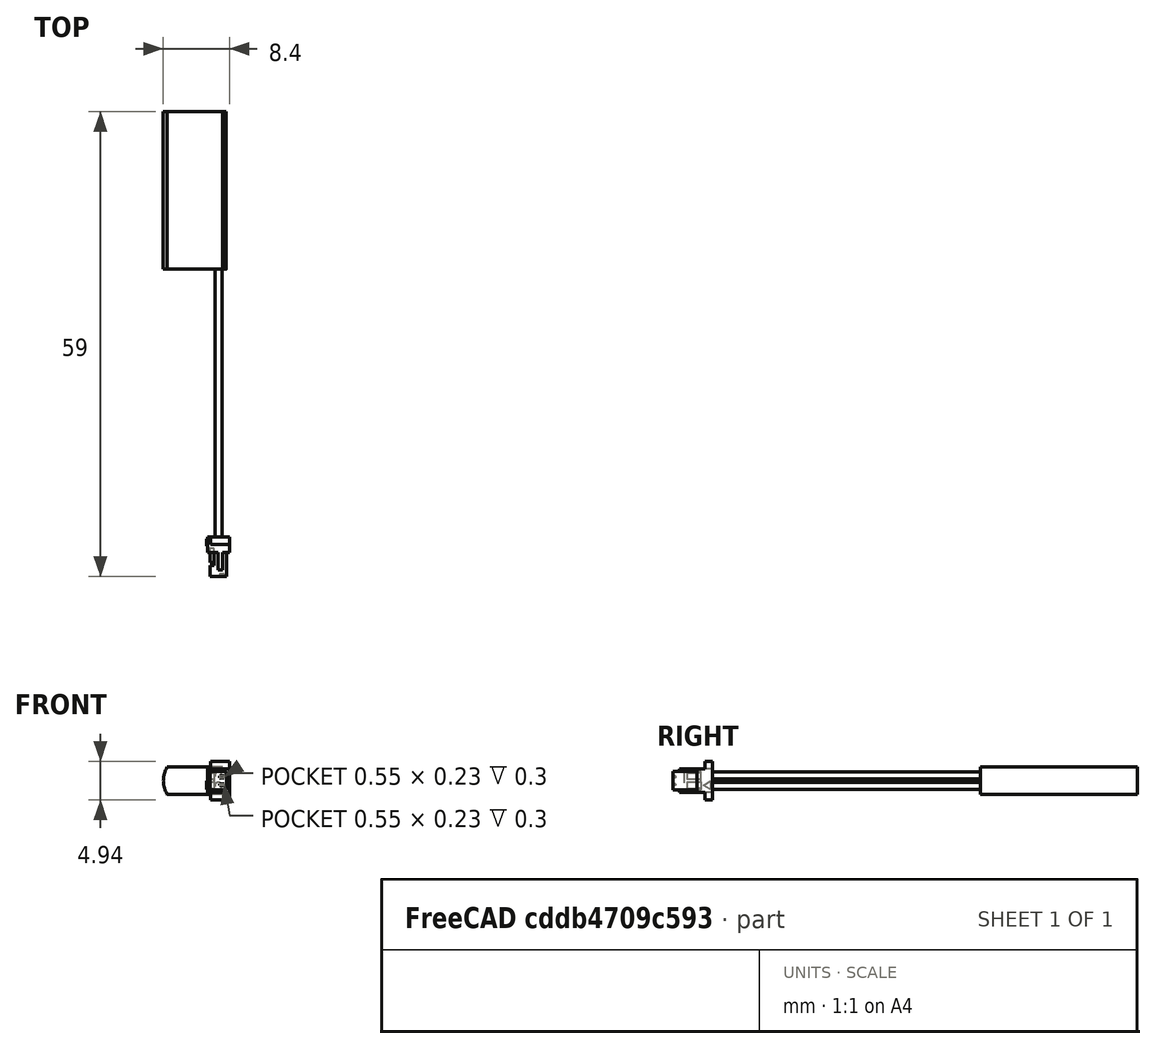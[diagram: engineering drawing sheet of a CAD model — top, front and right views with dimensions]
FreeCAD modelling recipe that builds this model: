
FCSTD DOCUMENT  (FreeCAD 2021.519R24301 +3652 (Git))
Label: ASR00072_40mAh
License: Other
objects: TechDraw::DrawViewDimension×4, Sketcher::SketchObject×3, PartDesign::Pad×3, TechDraw::DrawViewPart×2, TechDraw::DrawViewAnnotation×2, PartDesign::Pocket×1, PartDesign::Mirrored×1, PartDesign::Body×1, Part::Feature×1, Part::MultiFuse×1, TechDraw::DrawSVGTemplate×1, TechDraw::DrawPage×1, Mesh::Feature×1
note: 21 computed .brp shape members not serialized (recipe doc carries the construction recipe); baked Part::Feature solids carry a one-line shape summary decoded from their .brp

FEATURE [Sketcher::SketchObject] Sketch
  FullyConstrained = true
  MapMode = 5
  Support = -> [XY_Plane]
  sketch-geometry (4):
    g0: LineSegment StartX=-4 StartY=10 StartZ=0 EndX=4 EndY=10 EndZ=0
    g1: LineSegment StartX=4 StartY=10 StartZ=0 EndX=4 EndY=-10 EndZ=0
    g2: LineSegment StartX=4 StartY=-10 StartZ=0 EndX=-4 EndY=-10 EndZ=0
    g3: LineSegment StartX=-4 StartY=-10 StartZ=0 EndX=-4 EndY=10 EndZ=0
  constraints (10):
    c: Coincident(g0,g1)
    c: Coincident(g1,g2)
    c: Coincident(g2,g3)
    c: Coincident(g3,g0)
    c: Horizontal(g2)
    c: Vertical(g1)
    c: Symmetric(g0,g2,g-1)
    c: Symmetric(g0,g0,g-2)
    c: DistanceX(g0,g0) = 8
    c: DistanceY(g3,g3) = 20
FEATURE [PartDesign::Pad] Pad
  ClaimChildren = false
  Direction = (1,1,1)
  Fit = 0
  FitJoin = 0
  InnerFit = 0
  InnerFitJoin = 0
  InnerTaperAngle = 0
  InnerTaperAngleRev = 0
  Length = 3.5
  Length2 = 100
  Midplane = true
  NewSolid = false
  Profile = -> Sketch
  Suppress = false
  Type = 0
FEATURE [Sketcher::SketchObject] Sketch001
  ExternalGeometry = -> [Pad]
  FullyConstrained = true
  MapMode = 5
  Placement = pos=(0,10,0) rot=(0,0.707107,0.707107;3.14159rad)
  Support = -> [Pad]
  sketch-geometry (5):
    g0: ArcOfCircle CenterX=-0.6875 CenterY=-4e-16 CenterZ=0 NormalX=0 NormalY=0 NormalZ=1 AngleXU=0 Radius=3.3125 StartAngle=2.58499 EndAngle=3.69819
    g1: LineSegment [constr] StartX=-3.5 StartY=-1.75 StartZ=0 EndX=-3.5 EndY=1.75 EndZ=0
    g2: LineSegment StartX=-3.5 StartY=-1.75 StartZ=0 EndX=-5 EndY=-1.75 EndZ=0
    g3: LineSegment StartX=-3.5 StartY=1.75 StartZ=0 EndX=-5 EndY=1.75 EndZ=0
    g4: LineSegment StartX=-5 StartY=1.75 StartZ=0 EndX=-5 EndY=-1.75 EndZ=0
  constraints (15):
    c: PointOnObject(g0,g-5)
    c: PointOnObject(g0,g-4)
    c: Tangent(g0,g-3)
    c: Coincident(g1,g0)
    c: Coincident(g1,g0)
    c: Vertical(g1)
    c: Coincident(g2,g0)
    c: Horizontal(g2)
    c: Coincident(g3,g0)
    c: Horizontal(g3)
    c: Coincident(g4,g3)
    c: Coincident(g4,g2)
    c: Vertical(g4)
    c: DistanceX(g3,g-4) = 1
    c: DistanceX(g-4,g0) = 0.5
FEATURE [PartDesign::Pocket] Pocket
  BaseFeature = -> Pad
  ClaimChildren = false
  Fit = 0
  FitJoin = 0
  InnerFit = 0
  InnerFitJoin = 0
  InnerTaperAngle = 0
  InnerTaperAngleRev = 0
  Length = 5
  Length2 = 100
  NewSolid = false
  Profile = -> Sketch001
  Suppress = false
  Type = 1
FEATURE [PartDesign::Mirrored] Mirrored
  BaseFeature = -> Pocket
  CopyShape = true
  MirrorPlane = -> Sketch001 [V_Axis]
  NewSolid = false
  OriginalSubs = -> [Pocket]
  Originals = -> [Pocket]
  ParallelTransform = true
  SubTransform = true
  Suppress = false
FEATURE [PartDesign::Pad] Pad001
  BaseFeature = -> Mirrored
  ClaimChildren = false
  Direction = (1,1,1)
  Fit = 0
  FitJoin = 0
  InnerFit = 0
  InnerFitJoin = 0
  InnerTaperAngle = 0
  InnerTaperAngleRev = 0
  Length = 7.85
  Length2 = 100
  NewSolid = false
  Profile = -> Mirrored [Face8]
  Reversed = true
  Suppress = false
  Type = 0
FEATURE [Sketcher::SketchObject] Sketch002
  ExternalGeometry = -> [Pad001]
  FullyConstrained = true
  MapMode = 5
  Placement = pos=(0,-10,0) rot=(1,0,0;1.5708rad)
  Support = -> [Pad001]
  sketch-geometry (6):
    g0: Circle CenterX=3 CenterY=-0.65 CenterZ=0 NormalX=0 NormalY=0 NormalZ=1 AngleXU=0 Radius=0.45
    g1: Circle CenterX=3 CenterY=0.65 CenterZ=0 NormalX=0 NormalY=0 NormalZ=1 AngleXU=0 Radius=0.45
    g2: LineSegment [constr] StartX=3 StartY=0.65 StartZ=0 EndX=3 EndY=-0.65 EndZ=0
    g3: GeomPoint [constr] X=3 Y=-1.1 Z=0
    g4: GeomPoint [constr] X=3 Y=1.1 Z=0
    g5: LineSegment [constr] StartX=3 StartY=-0.65 StartZ=0 EndX=3.45 EndY=-0.65 EndZ=0
  constraints (13):
    c: Coincident(g2,g1)
    c: Coincident(g2,g0)
    c: Equal(g0,g1)
    c: Diameter(g0) = 0.9
    c: Symmetric(g0,g1,g-1)
    c: PointOnObject(g3,g2)
    c: PointOnObject(g4,g1)
    c: Symmetric(g3,g4,g-1)
    c: DistanceY(g-3,g3) = 0.65
    c: Coincident(g5,g0)
    c: PointOnObject(g5,g0)
    c: Horizontal(g5)
    c: DistanceX(g5,g-3) = 0.05
FEATURE [PartDesign::Pad] Pad002
  BaseFeature = -> Pad001
  ClaimChildren = false
  Direction = (1,1,1)
  Fit = 0
  FitJoin = 0
  InnerFit = 0
  InnerFitJoin = 0
  InnerTaperAngle = 0
  InnerTaperAngleRev = 0
  Length = 34
  Length2 = 100
  NewSolid = false
  Profile = -> Sketch002
  Suppress = false
  Type = 0
FEATURE [PartDesign::Body] Body
  AutoGroupSolids = false
  ExportMode = 0
  Group = -> [Sketch,Pad,Sketch001,Pocket,Mirrored,Pad001,Sketch002,Pad002]
  Origin = -> Origin
  Tip = -> Pad002
  _ExportChildren = -> [Pad,Pocket,Mirrored,Pad001,Pad002]
  _GroupVersion = 1
FEATURE [Part::Feature] Solid  label="Body007"
  Placement = pos=(1.71545,-46,8.5e-15) rot=(0,0,1;0rad)
  shape: bbox 2.9 x 5 x 4.94 mm, 60 faces (baked)
FEATURE [Part::MultiFuse] Fusion
  Shapes = -> [Body,Solid]
FEATURE [TechDraw::DrawSVGTemplate] Template
  Height = 210
  Orientation = 1
  Width = 297
FEATURE [TechDraw::DrawViewPart] View
  CoarseView = false
  Direction = (0,0,1)
  Focus = 100
  HardHidden = false
  IsoCount = 0
  IsoHidden = false
  IsoVisible = false
  LockPosition = false
  Perspective = false
  Rotation = 180
  Scale = 1.855
  ScaleType = 0
  SeamHidden = false
  SeamVisible = true
  SmoothHidden = false
  SmoothVisible = true
  Source = -> [Fusion]
  X = 178.5
  XDirection = (1,0,0)
  Y = 105
FEATURE [TechDraw::DrawViewPart] View001
  CoarseView = false
  Direction = (-1,0,0)
  Focus = 100
  HardHidden = false
  IsoCount = 0
  IsoHidden = false
  IsoVisible = false
  LockPosition = false
  Perspective = false
  Rotation = 90
  Scale = 1.855
  ScaleType = 0
  SeamHidden = false
  SeamVisible = true
  SmoothHidden = false
  SmoothVisible = true
  Source = -> [Fusion]
  X = 118.5
  XDirection = (0,-1,0)
  Y = 105
FEATURE [TechDraw::DrawViewAnnotation] Annotation
  Font = MS Shell Dlg 2
  LineSpace = 80
  LockPosition = false
  MaxWidth = -1
  Rotation = 0
  ScaleType = 0
  Text = SIDE VIEW
  TextSize = 6
  TextStyle = 0
  X = 118.5
  Y = 162
FEATURE [TechDraw::DrawViewAnnotation] Annotation001
  Font = MS Shell Dlg 2
  LineSpace = 80
  LockPosition = false
  MaxWidth = -1
  Rotation = 0
  ScaleType = 0
  Text = TOP VIEW
  TextSize = 6
  TextStyle = 0
  X = 178.5
  Y = 162
FEATURE [TechDraw::DrawViewDimension] Dimension
  Arbitrary = false
  ArbitraryTolerances = false
  EqualTolerance = true
  FormatSpec = %.1f
  FormatSpecOverTolerance = %+.1f
  FormatSpecUnderTolerance = %+.1f
  Inverted = false
  LockPosition = false
  MeasureType = 1
  OverTolerance = 0.5
  References2D = -> [View001]
  Rotation = 0
  ScaleType = 0
  TheoreticalExact = false
  Type = 1
  UnderTolerance = -0.5
  X = -31
  Y = -59
FEATURE [TechDraw::DrawViewDimension] Dimension001
  Arbitrary = false
  ArbitraryTolerances = false
  EqualTolerance = true
  FormatSpec = %.1f
  FormatSpecOverTolerance = %+.1f
  FormatSpecUnderTolerance = %+.1f
  Inverted = false
  LockPosition = false
  MeasureType = 1
  OverTolerance = 2
  References2D = -> [View]
  Rotation = 0
  ScaleType = 0
  TheoreticalExact = false
  Type = 1
  UnderTolerance = -2
  X = 24.371
  Y = -59
FEATURE [TechDraw::DrawViewDimension] Dimension002
  Arbitrary = false
  ArbitraryTolerances = false
  EqualTolerance = true
  FormatSpec = %.1f
  FormatSpecOverTolerance = %+.1f
  FormatSpecUnderTolerance = %+.1f
  Inverted = false
  LockPosition = false
  MeasureType = 1
  OverTolerance = 3
  References2D = -> [View]
  Rotation = 0
  ScaleType = 0
  TheoreticalExact = false
  Type = 2
  UnderTolerance = -3
  X = -24
  Y = -35.1725
FEATURE [TechDraw::DrawViewDimension] Dimension003
  Arbitrary = false
  ArbitraryTolerances = false
  EqualTolerance = true
  FormatSpec = %.1f
  FormatSpecOverTolerance = %+.1f
  FormatSpecUnderTolerance = %+.1f
  Inverted = false
  LockPosition = false
  MeasureType = 1
  OverTolerance = 5
  References2D = -> [View]
  Rotation = 0
  ScaleType = 0
  TheoreticalExact = false
  Type = 2
  UnderTolerance = -5
  X = -24
  Y = 14.9125
FEATURE [TechDraw::DrawPage] Page
  KeepUpdated = true
  NextBalloonIndex = 1
  ProjectionType = 0
  Template = -> Template
  Views = -> [View,View001,Annotation,Annotation001,Dimension,Dimension001,Dimension002,Dimension003]
FEATURE [Mesh::Feature] Mesh  label="Fusion (Meshed)"
